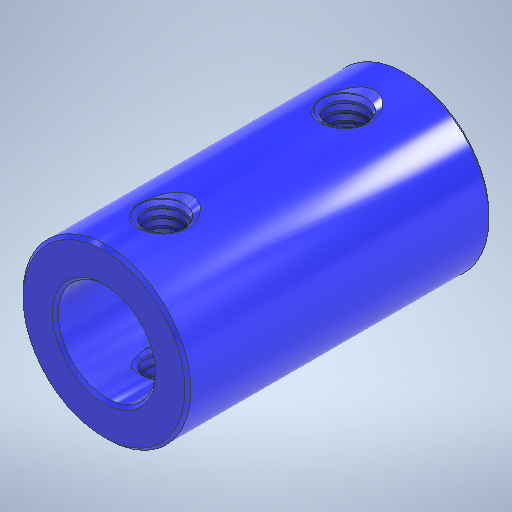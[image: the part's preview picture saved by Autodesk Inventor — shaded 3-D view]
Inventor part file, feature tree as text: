
AUTODESK INVENTOR PART (.ipt)
format: ipt  version: 2025.2 (Build 292293000, 293)  size: 938,496 bytes
history: native  units: in
note: dims shown in document units (in); Inventor stores cm internally (conversion verified against a paired STEP export)
features: thread x1
ambient origin geometry x8: Origin, YZ Plane, XZ Plane, XY Plane, X Axis, Y Axis, Z Axis, Center Point
bodies: Solid1 (feature_tree)
feature tree (1):
  thread  "Thread2"  [1 undecoded]
note: 1 required parameter value undecoded (feature->parameter linkage not recoverable at this tier; creation-order binding heuristic only, values carry confidence <= 0.55)
